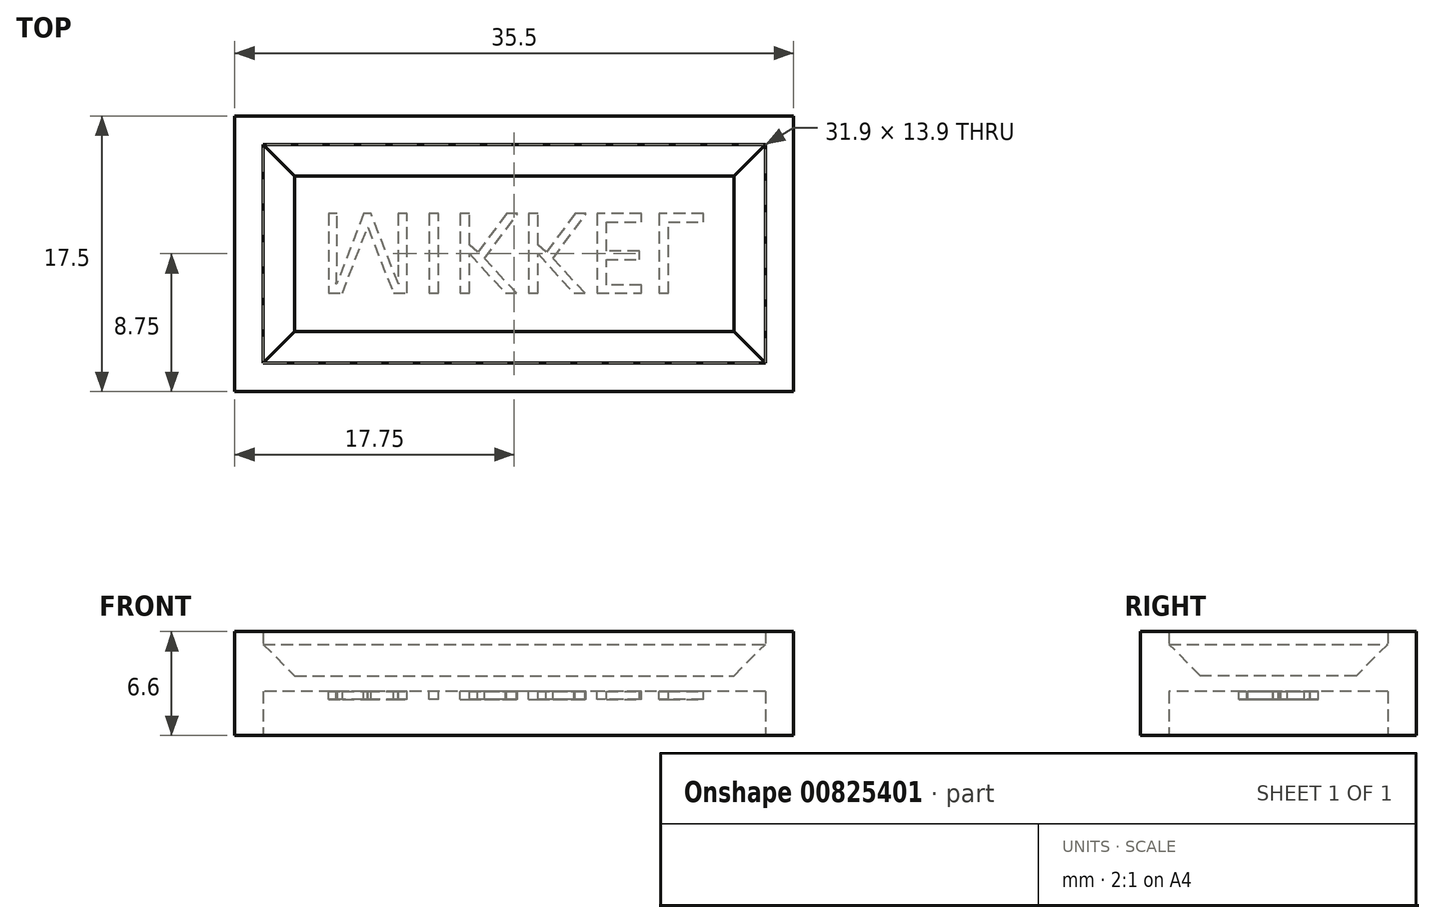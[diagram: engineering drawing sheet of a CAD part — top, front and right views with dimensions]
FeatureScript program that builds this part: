
annotation { "Feature Type Name" : "Feature", "Feature Type Description" : "" }
export const myFeature = defineFeature(function(context is Context, id is Id, definition is map)
    precondition{}
    {
        {
            var Q0;
            Q0=qCreatedBy(makeId("Top.planeOp"),FACE);
            var sketch = newSketch(context, id + "F0", { "sketchPlane" : qUnion([Q0])});
            skLineSegment(sketch, "E0.bottom", {"start": v(17.75, 8.75) * mm, "end": v(-17.75, 8.75) * mm});
            skLineSegment(sketch, "E0.top", {"start": v(17.75, -8.75) * mm, "end": v(-17.75, -8.75) * mm});
            skLineSegment(sketch, "E0.left", {"start": v(17.75, 8.75) * mm, "end": v(17.75, -8.75) * mm});
            skLineSegment(sketch, "E0.right", {"start": v(-17.75, 8.75) * mm, "end": v(-17.75, -8.75) * mm});
            skPoint(sketch, "E0.middle", {"position": v(0, 0) * mm});
            skLineSegment(sketch, "E1.0", {"start": v(-15.95, 6.95) * mm, "end": v(-15.95, -6.95) * mm});
            skLineSegment(sketch, "E1.1", {"start": v(15.95, 6.95) * mm, "end": v(-15.95, 6.95) * mm});
            skLineSegment(sketch, "E1.2", {"start": v(15.95, 6.95) * mm, "end": v(15.95, -6.95) * mm});
            skLineSegment(sketch, "E1.3", {"start": v(15.95, -6.95) * mm, "end": v(-15.95, -6.95) * mm});
            skSolve(sketch);
        }
        {
            var Q0;
            Q0=makeQuery(id+"F0.imprint","IMPRINT",FACE,{"disambiguationData":[TD([[makeQuery(id+"F0.imprint","IMPRINT",EDGE,{"derivedFrom":sQuery(id+"F0.wireOp",EDGE,"E1.0")}),1.0]])]});
            extrude(context, id + "F1", {"entities" : qUnion([Q0]), "endBound" : BoundingType.SYMMETRIC, "depth" : 1 * mm, "offsetDistance" : 25 * mm});
        }
        {
            var Q0;
            Q0=makeQuery(id+"F0.imprint","IMPRINT",FACE,{"disambiguationData":[TD([[makeQuery(id+"F0.imprint","IMPRINT",EDGE,{"derivedFrom":sQuery(id+"F0.wireOp",EDGE,"E0.bottom")}),1.0]])]});
            extrude(context, id + "F2", {"entities" : qUnion([Q0]), "operationType" : NewBodyOperationType.ADD, "endBound" : BoundingType.SYMMETRIC, "depth" : 6.6 * mm, "offsetDistance" : 25 * mm});
        }
        {
            var Q0;
            Q0=makeQuery(id+"F1.opExtrude","CAP_EDGE",EDGE,{"disambiguationData":[OSD([sQuery(id+"F0.wireOp",EDGE,"E1.1")])],"isStart":false});
            var Q1;
            Q1=makeQuery(id+"F1.opExtrude","CAP_EDGE",EDGE,{"disambiguationData":[OSD([sQuery(id+"F0.wireOp",EDGE,"E1.2")])],"isStart":false});
            var Q2;
            Q2=makeQuery(id+"F1.opExtrude","CAP_EDGE",EDGE,{"disambiguationData":[OSD([sQuery(id+"F0.wireOp",EDGE,"E1.3")])],"isStart":false});
            var Q3;
            Q3=makeQuery(id+"F1.opExtrude","CAP_EDGE",EDGE,{"disambiguationData":[OSD([sQuery(id+"F0.wireOp",EDGE,"E1.0")])],"isStart":false});
            var Q4;
            Q4=makeQuery(id+"F1.opExtrude","CAP_EDGE",EDGE,{"disambiguationData":[OSD([sQuery(id+"F0.wireOp",EDGE,"E1.3")])],"isStart":true});
            var Q5;
            Q5=makeQuery(id+"F1.opExtrude","CAP_EDGE",EDGE,{"disambiguationData":[OSD([sQuery(id+"F0.wireOp",EDGE,"E1.0")])],"isStart":true});
            var Q6;
            Q6=makeQuery(id+"F1.opExtrude","CAP_EDGE",EDGE,{"disambiguationData":[OSD([sQuery(id+"F0.wireOp",EDGE,"E1.1")])],"isStart":true});
            var Q7;
            Q7=makeQuery(id+"F1.opExtrude","CAP_EDGE",EDGE,{"disambiguationData":[OSD([sQuery(id+"F0.wireOp",EDGE,"E1.2")])],"isStart":true});
            chamfer(context, id + "F3", {"entities" : qUnion([Q0, Q1, Q2, Q3, Q4, Q5, Q6, Q7]), "width" : 2 * mm, "tangentPropagation" : true});
        }
        {
            var Q0;
            Q0=makeQuery(id+"F1.opExtrude","CAP_FACE",FACE,{"disambiguationData":[OSD([sQuery(id+"F0.wireOp",EDGE,"E1.0"),sQuery(id+"F0.wireOp",EDGE,"E1.1"),sQuery(id+"F0.wireOp",EDGE,"E1.2"),sQuery(id+"F0.wireOp",EDGE,"E1.3")])],"isStart":true});
            var sketch = newSketch(context, id + "F4", { "sketchPlane" : qUnion([Q0])});
            skText(sketch, "E2", { "text": "MIKKEL", "fontName": "OpenSans-Regular.ttf"});
            const initialGuessF4  = {"E2": [-0.0125, -0.00255, 1, 0, 0.0051]};
            skSetInitialGuess(sketch, initialGuessF4);
            skSolve(sketch);
        }
        {
            var Q0;
            Q0=qSketchRegion(id+"F4",true);
            extrude(context, id + "F5", {"entities" : qUnion([Q0]), "operationType" : NewBodyOperationType.ADD, "depth" : 0.5 * mm, "offsetDistance" : 25 * mm});
        }
    });
